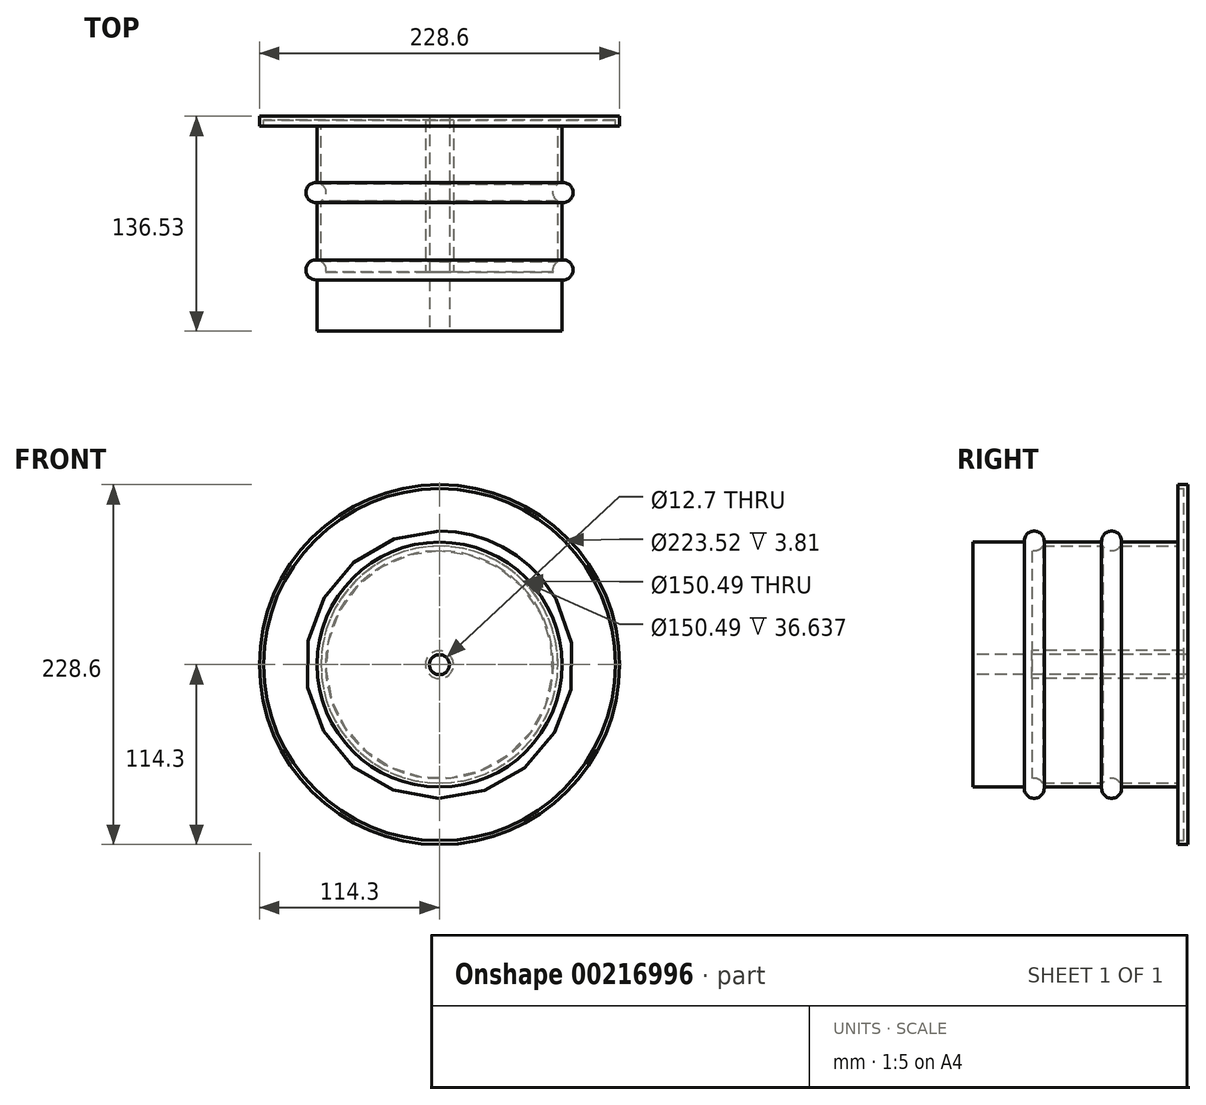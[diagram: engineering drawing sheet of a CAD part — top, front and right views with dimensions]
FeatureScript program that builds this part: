
annotation { "Feature Type Name" : "Feature", "Feature Type Description" : "" }
export const myFeature = defineFeature(function(context is Context, id is Id, definition is map)
    precondition{}
    {
        {
            var Q0;
            Q0=qCreatedBy(makeId("Front.planeOp"),FACE);
            var sketch = newSketch(context, id + "F0", { "sketchPlane" : qUnion([Q0])});
            skCircle(sketch, "E0", {"center": v(0, 0) * mm, "radius": 77.79 * mm});
            skCircle(sketch, "E1", {"center": v(0, 0) * mm, "radius": 114.3 * mm});
            skSolve(sketch);
        }
        {
            var Q0;
            Q0=makeQuery(id+"F0.imprint","IMPRINT",FACE,{"disambiguationData":[TD([[makeQuery(id+"F0.imprint","IMPRINT",EDGE,{"derivedFrom":sQuery(id+"F0.wireOp",EDGE,"E0")}),-1.0]])]});
            extrude(context, id + "F1", {"entities" : qUnion([Q0]), "depth" : 6.35 * mm});
        }
        {
            var Q0;
            Q0=makeQuery(id+"F0.imprint","IMPRINT",FACE,{"disambiguationData":[TD([[makeQuery(id+"F0.imprint","IMPRINT",EDGE,{"derivedFrom":sQuery(id+"F0.wireOp",EDGE,"E0")}),1.0]])]});
            extrude(context, id + "F2", {"entities" : qUnion([Q0]), "operationType" : NewBodyOperationType.ADD, "depth" : 203.2 * mm});
        }
        {
            var Q0;
            Q0=makeQuery(id+"F2.opExtrude","CAP_FACE",FACE,{"disambiguationData":[OSD([sQuery(id+"F0.wireOp",EDGE,"E0")])],"isStart":false});
            extrude(context, id + "F3", {"entities" : qUnion([Q0]), "operationType" : NewBodyOperationType.REMOVE, "oppositeDirection" : true, "depth" : 101.6 * mm});
        }
        {
            var Q0;
            Q0=makeQuery(id+"F3.boolean.opBoolean","COPY",FACE,{"derivedFrom":makeQuery(id+"F3.opExtrude","CAP_FACE",FACE,{"disambiguationData":[OSD([sQuery(id+"F0.wireOp",EDGE,"E0")])],"isStart":false})});
            var sketch = newSketch(context, id + "F4", { "sketchPlane" : qUnion([Q0])});
            skCircle(sketch, "E2", {"center": v(0, 0) * mm, "radius": 6.35 * mm});
            skSolve(sketch);
        }
        {
            var Q0;
            Q0=makeQuery(id+"F4.imprint","IMPRINT",FACE,{"disambiguationData":[TD([[makeQuery(id+"F4.imprint","IMPRINT",EDGE,{"derivedFrom":sQuery(id+"F4.wireOp",EDGE,"E2")}),1.0]])]});
            extrude(context, id + "F5", {"entities" : qUnion([Q0]), "operationType" : NewBodyOperationType.REMOVE, "endBound" : BoundingType.THROUGH_ALL, "oppositeDirection" : true, "depth" : 25.4 * mm});
        }
        {
            var Q0;
            Q0=makeQuery(id+"F1.opExtrude","CAP_FACE",FACE,{"disambiguationData":[OSD([sQuery(id+"F0.wireOp",EDGE,"E0"),sQuery(id+"F0.wireOp",EDGE,"E1")])],"isStart":false});
            shell(context, id + "F6", {"entities" : qUnion([Q0]), "thickness" : 2.54 * mm});
        }
        {
            var Q0;
            Q0=makeQuery(id+"F3.boolean.opBoolean","COPY",FACE,{"derivedFrom":makeQuery(id+"F3.opExtrude","CAP_FACE",FACE,{"disambiguationData":[OSD([sQuery(id+"F0.wireOp",EDGE,"E0")])],"isStart":false})});
            extrude(context, id + "F7", {"entities" : qUnion([Q0]), "operationType" : NewBodyOperationType.ADD, "depth" : 9.52 * mm});
        }
        {
            var Q0;
            Q0=makeQuery(id+"F7.opExtrude","CAP_FACE",FACE,{"disambiguationData":[OSD([sQuery(id+"F0.wireOp",EDGE,"E0")])],"isStart":false});
            extrude(context, id + "F8", {"entities" : qUnion([Q0]), "operationType" : NewBodyOperationType.ADD, "depth" : 25.4 * mm});
        }
        {
            var Q0;
            Q0=qCreatedBy(makeId("Right.planeOp"),FACE);
            var sketch = newSketch(context, id + "F9", { "sketchPlane" : qUnion([Q0])});
            skCircle(sketch, "E3", {"center": v(-97.58, 78.52) * mm, "radius": 6.35 * mm});
            skCircle(sketch, "E4", {"center": v(-48.43, 78.52) * mm, "radius": 6.35 * mm});
            skSolve(sketch);
        }
        {
            var Q0;
            Q0=makeQuery(id+"F9.imprint","IMPRINT",FACE,{"disambiguationData":[TD([[makeQuery(id+"F9.imprint","IMPRINT",EDGE,{"derivedFrom":sQuery(id+"F9.wireOp",EDGE,"E4")}),1.0]])]});
            var Q1;
            Q1=makeQuery(id+"F9.imprint","IMPRINT",FACE,{"disambiguationData":[TD([[makeQuery(id+"F9.imprint","IMPRINT",EDGE,{"derivedFrom":sQuery(id+"F9.wireOp",EDGE,"E3")}),1.0]])]});
            var Q2;
            Q2=makeQuery(id+"F8.opExtrude","CAP_EDGE",EDGE,{"disambiguationData":[OSD([sQuery(id+"F0.wireOp",EDGE,"E0")])],"isStart":false});
            revolve(context, id + "F10", {"operationType" : NewBodyOperationType.ADD, "entities" : qUnion([Q0, Q1]), "axis" : qUnion([Q2]), "revolveType" : RevolveType.FULL});
        }
    });
